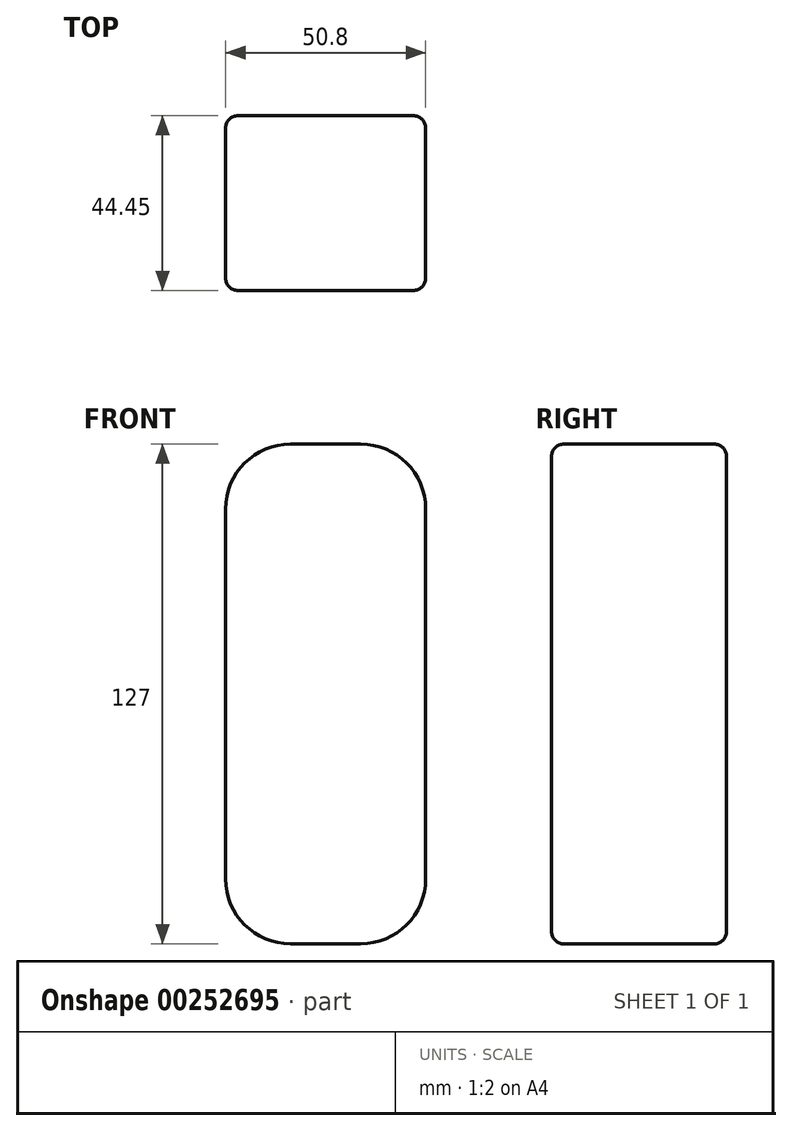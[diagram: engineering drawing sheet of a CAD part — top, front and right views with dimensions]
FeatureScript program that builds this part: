
annotation { "Feature Type Name" : "Feature", "Feature Type Description" : "" }
export const myFeature = defineFeature(function(context is Context, id is Id, definition is map)
    precondition{}
    {
        {
            var Q0;
            Q0=qCreatedBy(makeId("Front.planeOp"),FACE);
            var sketch = newSketch(context, id + "F0", { "sketchPlane" : qUnion([Q0])});
            skLineSegment(sketch, "E0.bottom", {"start": v(-8.89, 63.5) * mm, "end": v(8.9, 63.5) * mm});
            skLineSegment(sketch, "E0.top", {"start": v(-8.9, -63.5) * mm, "end": v(8.89, -63.5) * mm});
            skLineSegment(sketch, "E0.left", {"start": v(-25.4, 46.99) * mm, "end": v(-25.4, -47) * mm});
            skLineSegment(sketch, "E0.right", {"start": v(25.4, 46.99) * mm, "end": v(25.4, -47) * mm});
            skPoint(sketch, "E0.middle", {"position": v(0, 0) * mm});
            skPoint(sketch, "E1.visualSharp", {"position": v(-25.4, 63.5) * mm});
            skArc(sketch, "E1.filletArc", {"start": v(-8.89, 63.5) * mm, "mid": v(-20.56, 58.66) * mm, "end": v(-25.4, 46.99) * mm});
            skPoint(sketch, "E2.visualSharp", {"position": v(25.4, 63.5) * mm});
            skArc(sketch, "E2.filletArc", {"start": v(25.4, 46.99) * mm, "mid": v(20.56, 58.66) * mm, "end": v(8.9, 63.5) * mm});
            skPoint(sketch, "E3.visualSharp", {"position": v(-25.4, -63.5) * mm});
            skArc(sketch, "E3.filletArc", {"start": v(-25.4, -47) * mm, "mid": v(-20.56, -58.66) * mm, "end": v(-8.9, -63.5) * mm});
            skPoint(sketch, "E4.visualSharp", {"position": v(25.4, -63.5) * mm});
            skArc(sketch, "E4.filletArc", {"start": v(8.89, -63.5) * mm, "mid": v(20.56, -58.66) * mm, "end": v(25.4, -47) * mm});
            skSolve(sketch);
        }
        {
            var Q0;
            Q0 = qSketchRegion(id + "F0", true);
            extrude(context, id + "F1", {"entities" : qUnion([Q0]), "depth" : 44.45 * mm});
        }
        {
            var Q0;
            Q0=makeQuery(id+"F1.opExtrude","SWEPT_FACE",FACE,{"disambiguationData":[OSD([sQuery(id+"F0.wireOp",EDGE,"E3.filletArc")])]});
            var Q1;
            Q1=makeQuery(id+"F1.opExtrude","SWEPT_FACE",FACE,{"disambiguationData":[OSD([sQuery(id+"F0.wireOp",EDGE,"E4.filletArc")])]});
            fillet(context, id + "F2", {"entities" : qUnion([Q0, Q1]), "radius" : 3.17 * mm, "tangentPropagation" : true, "allowEdgeOverflow" : false});
        }
    });
